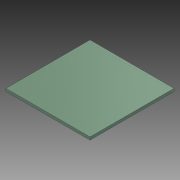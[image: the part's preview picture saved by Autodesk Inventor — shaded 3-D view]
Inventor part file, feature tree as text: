
AUTODESK INVENTOR PART (.ipt)
format: ipt  version: 2013 (Build 170138000, 138)  size: 69,632 bytes
history: native  units: mm
features: extrude x1, sketch x1
ambient origin geometry x8: Origin, YZ Plane, XZ Plane, XY Plane, X Axis, Y Axis, Z Axis, Center Point
bodies: Volumenkörper1 (feature_tree)
feature tree (2):
  extrude  "Extrusion1"  Depth=6.0mm
  sketch  "Skizze1"  dims[d0=6.0mm d1=6.0mm d2=0.2mm d3=0.0mm]
